# Revit family: Вазон для цветов «Хай-тек квадро»
name_source: partatom
category: Антураж
revit_build: Autodesk Revit 2017 (Build: 20160225_1515(x64)
units: mm (PartAtom-declared; Revit-internal decimal feet)

## family parameters
Всегда вертикально = Да
Источник визуального образа = Геометрия семейства
На основе рабочей плоскости = Нет
Общий = Нет
При загрузке вырезать с полостями = Нет
Точка расчета площади = Нет

## types (4) — shared parameters
ADSK_Код изделия = 6770
ADSK_Наименование = Вазон для цветов «Хай-тек квадро»
URL = https://hobbyka.ru
АDSK_Материал вазона = Сталь, хромированная
Изготовитель = ООО "Хоббика"
zero-valued in all types: Высота

## per-type parameters (varying)
| type | ADSK_Размер_Высота | ADSK_Размер_Ширина | b | Стоимость |
| Вазон для цветов «Хай-тек квадро» 300х300х300 | 300 мм | 300 мм | 139 мм | 6885 $ |
| Вазон для цветов «Хай-тек квадро» 400х400х400 | 400 мм | 400 мм | 189 мм | 11880 $ |
| Вазон для цветов «Хай-тек квадро» 500х500х500 | 500 мм | 500 мм | 239 мм | 18225 $ |
| Вазон для цветов «Хай-тек квадро» 600х600х600 | 600 мм | 600 мм | 289 мм | 25886 $ |
